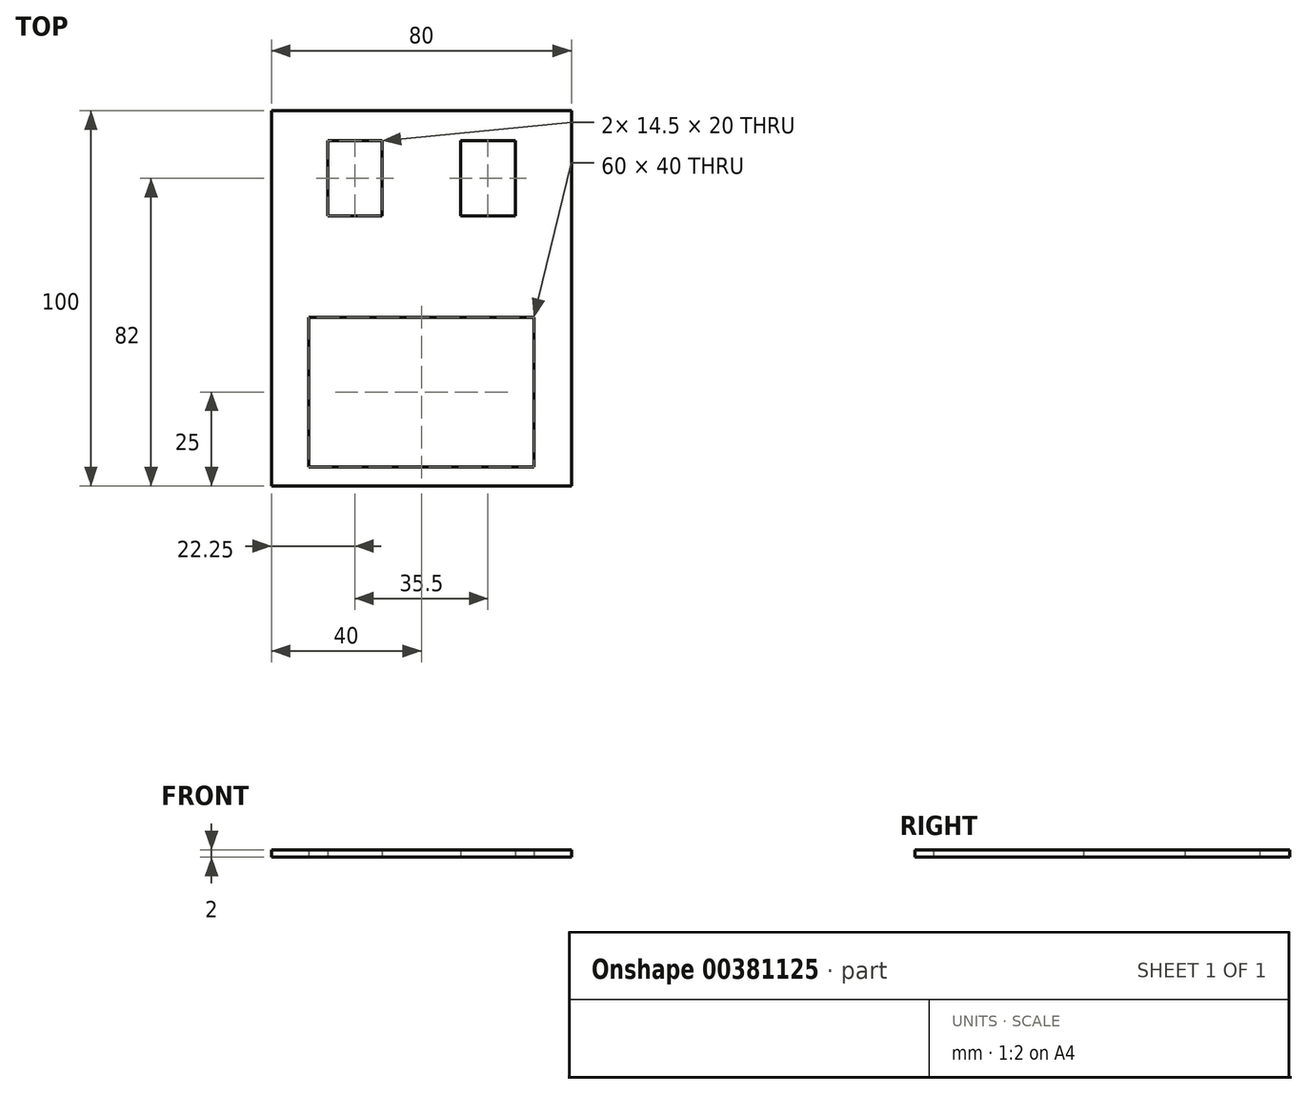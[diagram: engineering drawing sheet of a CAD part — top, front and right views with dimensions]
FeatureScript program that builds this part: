
annotation { "Feature Type Name" : "Feature", "Feature Type Description" : "" }
export const myFeature = defineFeature(function(context is Context, id is Id, definition is map)
    precondition{}
    {
        {
            var Q0;
            Q0=qCreatedBy(makeId("Top.planeOp"),FACE);
            var sketch = newSketch(context, id + "F0", { "sketchPlane" : qUnion([Q0])});
            skLineSegment(sketch, "E0.bottom", {"start": v(40, 50) * mm, "end": v(-40, 50) * mm});
            skLineSegment(sketch, "E0.top", {"start": v(40, -50) * mm, "end": v(-40, -50) * mm});
            skLineSegment(sketch, "E0.left", {"start": v(40, 50) * mm, "end": v(40, -50) * mm});
            skLineSegment(sketch, "E0.right", {"start": v(-40, 50) * mm, "end": v(-40, -50) * mm});
            skPoint(sketch, "E0.middle", {"position": v(0, 0) * mm});
            skLineSegment(sketch, "E1.bottom", {"start": v(30, -45) * mm, "end": v(-30, -45) * mm});
            skLineSegment(sketch, "E1.top", {"start": v(30, -5) * mm, "end": v(-30, -5) * mm});
            skLineSegment(sketch, "E1.left", {"start": v(30, -45) * mm, "end": v(30, -5) * mm});
            skLineSegment(sketch, "E1.right", {"start": v(-30, -45) * mm, "end": v(-30, -5) * mm});
            skPoint(sketch, "E1.middle", {"position": v(0, -25) * mm});
            skLineSegment(sketch, "E2.bottom", {"start": v(-10.5, 22) * mm, "end": v(-25, 22) * mm});
            skLineSegment(sketch, "E2.top", {"start": v(-10.5, 42) * mm, "end": v(-25, 42) * mm});
            skLineSegment(sketch, "E2.left", {"start": v(-10.5, 22) * mm, "end": v(-10.5, 42) * mm});
            skLineSegment(sketch, "E2.right", {"start": v(-25, 22) * mm, "end": v(-25, 42) * mm});
            skPoint(sketch, "E2.middle", {"position": v(-17.75, 32) * mm});
            skLineSegment(sketch, "E3.bottom", {"start": v(25, 22) * mm, "end": v(10.5, 22) * mm});
            skLineSegment(sketch, "E3.top", {"start": v(25, 42) * mm, "end": v(10.5, 42) * mm});
            skLineSegment(sketch, "E3.left", {"start": v(25, 22) * mm, "end": v(25, 42) * mm});
            skLineSegment(sketch, "E3.right", {"start": v(10.5, 22) * mm, "end": v(10.5, 42) * mm});
            skPoint(sketch, "E3.middle", {"position": v(17.75, 32) * mm});
            skSolve(sketch);
        }
        {
            var Q0;
            Q0 = qSketchRegion(id + "F0", true);
            extrude(context, id + "F1", {"entities" : qUnion([Q0]), "depth" : 2 * mm});
        }
    });
